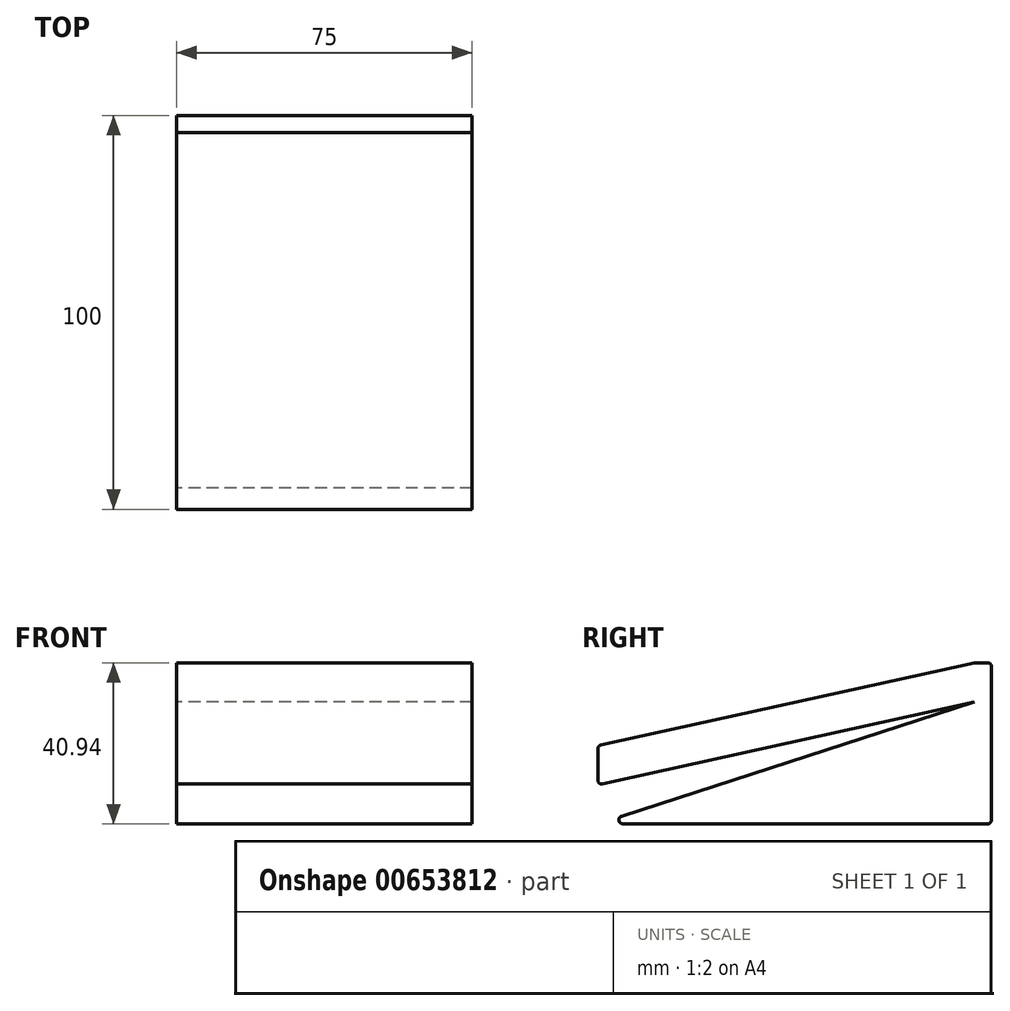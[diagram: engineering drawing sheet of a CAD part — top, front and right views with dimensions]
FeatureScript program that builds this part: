
annotation { "Feature Type Name" : "Feature", "Feature Type Description" : "" }
export const myFeature = defineFeature(function(context is Context, id is Id, definition is map)
    precondition{}
    {
        {
            var Q0;
            Q0=qCreatedBy(makeId("Right.planeOp"),FACE);
            var sketch = newSketch(context, id + "F0", { "sketchPlane" : qUnion([Q0])});
            skLineSegment(sketch, "E0", {"start": v(0, 0) * mm, "end": v(-100, 0) * mm});
            skLineSegment(sketch, "E1", {"start": v(-100, 0) * mm, "end": v(-4.31, 30.94) * mm});
            skLineSegment(sketch, "E2", {"start": v(-4.31, 30.94) * mm, "end": v(-100, 9.87) * mm});
            skLineSegment(sketch, "E3", {"start": v(-100, 9.87) * mm, "end": v(-100, 19.87) * mm});
            skLineSegment(sketch, "E4", {"start": v(-100, 19.87) * mm, "end": v(-4.31, 40.94) * mm});
            skLineSegment(sketch, "E5", {"start": v(-4.31, 40.94) * mm, "end": v(0, 40.94) * mm});
            skLineSegment(sketch, "E6", {"start": v(0, 40.94) * mm, "end": v(0, 0) * mm});
            skSolve(sketch);
        }
        {
            var Q0;
            Q0 = qSketchRegion(id + "F0", true);
            extrude(context, id + "F1", {"entities" : qUnion([Q0]), "depth" : 75 * mm, "offsetDistance" : 25 * mm});
        }
        {
            var Q0;
            Q0=makeQuery(id+"F1.opExtrude","SWEPT_EDGE",EDGE,{"disambiguationData":[OSD([sQuery(id+"F0.wireOp",EDGE,"E2"),sQuery(id+"F0.wireOp",EDGE,"E3")])]});
            var Q1;
            Q1=makeQuery(id+"F1.opExtrude","SWEPT_EDGE",EDGE,{"disambiguationData":[OSD([sQuery(id+"F0.wireOp",EDGE,"E3"),sQuery(id+"F0.wireOp",EDGE,"E4")])]});
            var Q2;
            Q2=makeQuery(id+"F1.opExtrude","SWEPT_EDGE",EDGE,{"disambiguationData":[OSD([sQuery(id+"F0.wireOp",EDGE,"E0"),sQuery(id+"F0.wireOp",EDGE,"E1")])]});
            var Q3;
            Q3=makeQuery(id+"F1.opExtrude","SWEPT_EDGE",EDGE,{"disambiguationData":[OSD([sQuery(id+"F0.wireOp",EDGE,"E5"),sQuery(id+"F0.wireOp",EDGE,"E6")])]});
            var Q4;
            Q4=makeQuery(id+"F1.opExtrude","SWEPT_EDGE",EDGE,{"disambiguationData":[OSD([sQuery(id+"F0.wireOp",EDGE,"E0"),sQuery(id+"F0.wireOp",EDGE,"E6")])]});
            fillet(context, id + "F2", {"entities" : qUnion([Q0, Q1, Q2, Q3, Q4]), "radius" : 1 * mm, "tangentPropagation" : true, "allowEdgeOverflow" : false});
        }
    });
